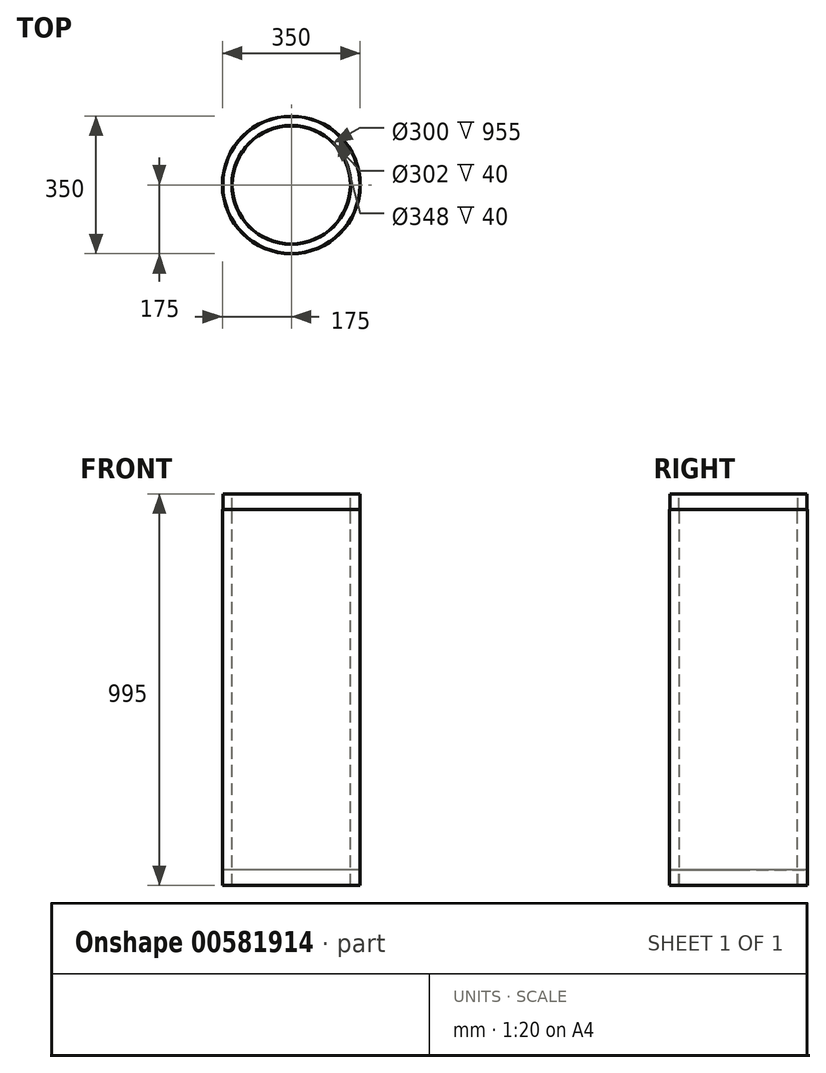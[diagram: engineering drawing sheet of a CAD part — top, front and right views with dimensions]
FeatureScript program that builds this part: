
annotation { "Feature Type Name" : "Feature", "Feature Type Description" : "" }
export const myFeature = defineFeature(function(context is Context, id is Id, definition is map)
    precondition{}
    {
        {
            var Q0;
            Q0=qCreatedBy(makeId("Front.planeOp"),FACE);
            var sketch = newSketch(context, id + "F0", { "sketchPlane" : qUnion([Q0])});
            skLineSegment(sketch, "E0", {"start": v(0, 345.75) * mm, "end": v(0, -558.03) * mm, "construction": true});
            skLineSegment(sketch, "E1", {"start": v(-150, -518.84) * mm, "end": v(-150, 436.16) * mm});
            skLineSegment(sketch, "E2", {"start": v(-150, 436.16) * mm, "end": v(-151, 436.16) * mm});
            skLineSegment(sketch, "E3", {"start": v(-151, 436.16) * mm, "end": v(-151, 476.16) * mm});
            skLineSegment(sketch, "E4", {"start": v(-151, 476.16) * mm, "end": v(-174, 476.16) * mm});
            skLineSegment(sketch, "E5", {"start": v(-174, 476.16) * mm, "end": v(-174, 436.16) * mm});
            skLineSegment(sketch, "E6", {"start": v(-174, 436.16) * mm, "end": v(-175, 436.16) * mm});
            skLineSegment(sketch, "E7", {"start": v(-175, 436.16) * mm, "end": v(-175, -518.84) * mm});
            skLineSegment(sketch, "E8", {"start": v(-175, -518.84) * mm, "end": v(-174, -518.84) * mm});
            skLineSegment(sketch, "E9", {"start": v(-174, -518.84) * mm, "end": v(-174, -478.84) * mm});
            skLineSegment(sketch, "E10", {"start": v(-174, -478.84) * mm, "end": v(-151, -478.84) * mm});
            skLineSegment(sketch, "E11", {"start": v(-151, -478.84) * mm, "end": v(-151, -518.84) * mm});
            skLineSegment(sketch, "E12", {"start": v(-151, -518.84) * mm, "end": v(-150, -518.84) * mm});
            skSolve(sketch);
        }
        {
            var Q0;
            Q0=qSketchRegion(id+"F0",true);
            var Q1;
            Q1=sQuery(id+"F0.wireOp",EDGE,"E0");
            revolve(context, id + "F1", {"entities" : qUnion([Q0]), "axis" : qUnion([Q1]), "revolveType" : RevolveType.FULL});
        }
    });
